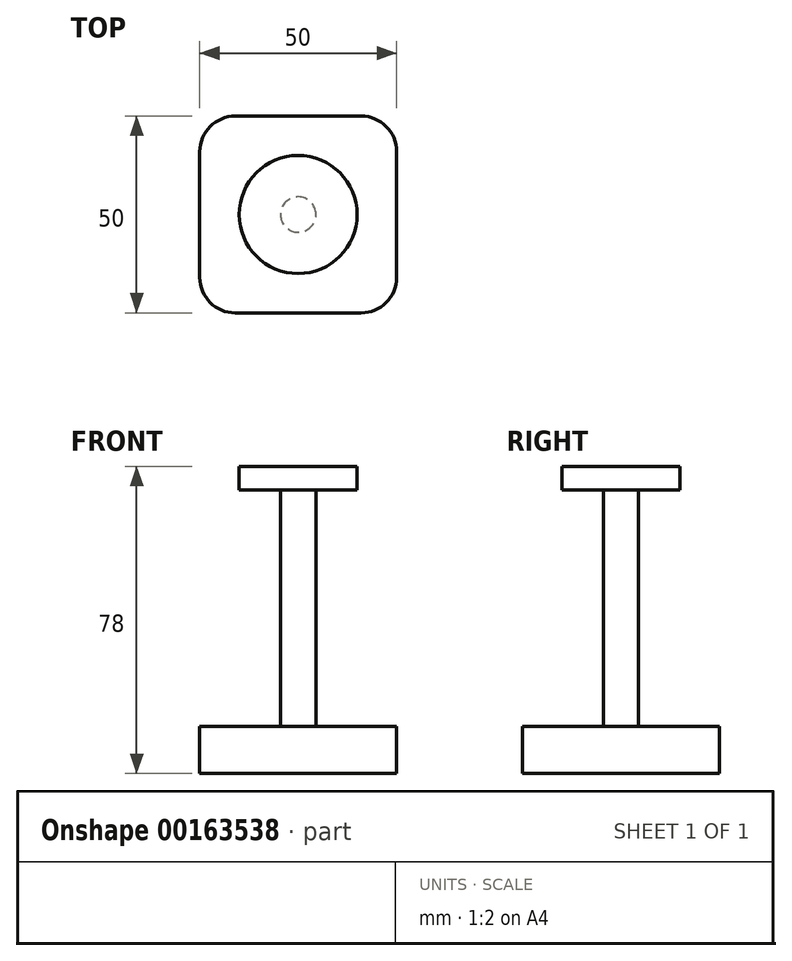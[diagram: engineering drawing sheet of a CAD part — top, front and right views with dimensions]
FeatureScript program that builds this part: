
annotation { "Feature Type Name" : "Feature", "Feature Type Description" : "" }
export const myFeature = defineFeature(function(context is Context, id is Id, definition is map)
    precondition{}
    {
        {
            var Q0;
            Q0=qCreatedBy(makeId("Front.planeOp"),FACE);
            var sketch = newSketch(context, id + "F0", { "sketchPlane" : qUnion([Q0])});
            skLineSegment(sketch, "E0.bottom", {"start": v(-25, 0) * mm, "end": v(25, 0) * mm});
            skLineSegment(sketch, "E0.top", {"start": v(-25, 12) * mm, "end": v(25, 12) * mm});
            skLineSegment(sketch, "E0.left", {"start": v(-25, 0) * mm, "end": v(-25, 12) * mm});
            skLineSegment(sketch, "E0.right", {"start": v(25, 0) * mm, "end": v(25, 12) * mm});
            skLineSegment(sketch, "E1", {"start": v(0, 0) * mm, "end": v(0, 78) * mm});
            skLineSegment(sketch, "E2.bottom", {"start": v(-4.5, 12) * mm, "end": v(4.5, 12) * mm});
            skLineSegment(sketch, "E2.top", {"start": v(-4.5, 72) * mm, "end": v(4.5, 72) * mm});
            skLineSegment(sketch, "E2.left", {"start": v(-4.5, 12) * mm, "end": v(-4.5, 72) * mm});
            skLineSegment(sketch, "E2.right", {"start": v(4.5, 12) * mm, "end": v(4.5, 72) * mm});
            skPoint(sketch, "E2.middle", {"position": v(0, 42) * mm});
            skLineSegment(sketch, "E3.bottom", {"start": v(15, 78) * mm, "end": v(-15, 78) * mm});
            skLineSegment(sketch, "E3.top", {"start": v(15, 72) * mm, "end": v(-15, 72) * mm});
            skLineSegment(sketch, "E3.left", {"start": v(15, 78) * mm, "end": v(15, 72) * mm});
            skLineSegment(sketch, "E3.right", {"start": v(-15, 78) * mm, "end": v(-15, 72) * mm});
            skSolve(sketch);
        }
        {
            var Q0;
            Q0=makeQuery(id+"F0.imprint","IMPRINT",FACE,{"disambiguationData":[TD([[makeQuery(id+"F0.imprint","IMPRINT",EDGE,{"derivedFrom":sQuery(id+"F0.wireOp",EDGE,"E0.bottom")}),1.0]])]});
            extrude(context, id + "F1", {"entities" : qUnion([Q0]), "endBound" : BoundingType.SYMMETRIC, "depth" : 50 * mm});
        }
        {
            var Q0;
            {var subQ5=sQuery(id+"F0.wireOp",EDGE,"E2.right");Q0=makeQuery(id+"F0.imprint","IMPRINT",FACE,{"disambiguationData":[TD([[makeQuery(id+"F0.imprint","IMPRINT",EDGE,{"derivedFrom":subQ5}),1.0]])]});}
            var Q1;
            {var subQ4=sQuery(id+"F0.wireOp",EDGE,"E3.left");Q1=makeQuery(id+"F0.imprint","IMPRINT",FACE,{"disambiguationData":[TD([[makeQuery(id+"F0.imprint","IMPRINT",EDGE,{"derivedFrom":subQ4}),-1.0]])]});}
            var Q2;
            Q2=sQuery(id+"F0.wireOp",EDGE,"E1");
            revolve(context, id + "F2", {"entities" : qUnion([Q0, Q1]), "axis" : qUnion([Q2]), "revolveType" : RevolveType.FULL});
        }
        {
            var Q0;
            Q0=makeQuery(id+"F1.opExtrude","CAP_EDGE",EDGE,{"disambiguationData":[OSD([sQuery(id+"F0.wireOp",EDGE,"E0.left")])],"isStart":false});
            var Q1;
            Q1=makeQuery(id+"F1.opExtrude","CAP_EDGE",EDGE,{"disambiguationData":[OSD([sQuery(id+"F0.wireOp",EDGE,"E0.right")])],"isStart":false});
            var Q2;
            Q2=makeQuery(id+"F1.opExtrude","CAP_EDGE",EDGE,{"disambiguationData":[OSD([sQuery(id+"F0.wireOp",EDGE,"E0.right")])],"isStart":true});
            var Q3;
            Q3=makeQuery(id+"F1.opExtrude","CAP_EDGE",EDGE,{"disambiguationData":[OSD([sQuery(id+"F0.wireOp",EDGE,"E0.left")])],"isStart":true});
            fillet(context, id + "F3", {"entities" : qUnion([Q0, Q1, Q2, Q3]), "radius" : 9 * mm, "tangentPropagation" : true, "allowEdgeOverflow" : false});
        }
    });
